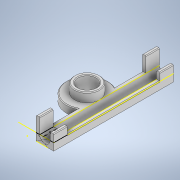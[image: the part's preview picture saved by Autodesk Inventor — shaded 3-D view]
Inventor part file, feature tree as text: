
AUTODESK INVENTOR PART (.ipt)
format: ipt  version: 2020 (Build 240168000, 168)  size: 205,824 bytes
history: native  units: mm
features: extrude x6, sketch x6, mirror x1, chamfer x1
ambient origin geometry x8: Origin, YZ Plane, XZ Plane, XY Plane, X Axis, Y Axis, Z Axis, Center Point
bodies: Solid1 (feature_tree)
feature tree (14):
  extrude  "Extrusion1"  Depth=10.0mm
  extrude  "Extrusion2"  Depth=5.0mm TaperAngle=0.0deg
  sketch  "Sketch3"  dims[d5=80.0mm d6=5.0mm d7=0.0mm]
  extrude  "Extrusion3"  Depth=5.0mm TaperAngle=0.0deg
  sketch  "Sketch5"  dims[d11=9.0mm d12=10.0mm d13=0.0mm]
  extrude  "Extrusion4"  TaperAngle=0.0deg  [1 undecoded]
  extrude  "Extrusion5"  Depth=10.0mm TaperAngle=0.0deg
  mirror  "Mirror1"
  extrude  "Extrusion6"  Depth=6.0mm TaperAngle=0.0deg
  chamfer  "Chamfer1"  Distance=0.5mm Angle=45.0deg
  sketch  "Sketch1"  dims[d0=27.6mm d1=10.0mm]
  sketch  "Sketch2"  dims[d2=12.0mm d3=5.0mm d4=0.0mm]
  sketch  "Sketch4"  dims[d8=7.0mm d9=0.0mm d10=0.0mm]
  sketch  "Sketch6"  dims[d14=5.0mm d15=0.0mm d16=6.0mm d17=0.0mm d18=0.5mm d19=2.0mm d20=45.0deg]
note: 1 required parameter value undecoded (feature->parameter linkage not recoverable at this tier; creation-order binding heuristic only, values carry confidence <= 0.55)
